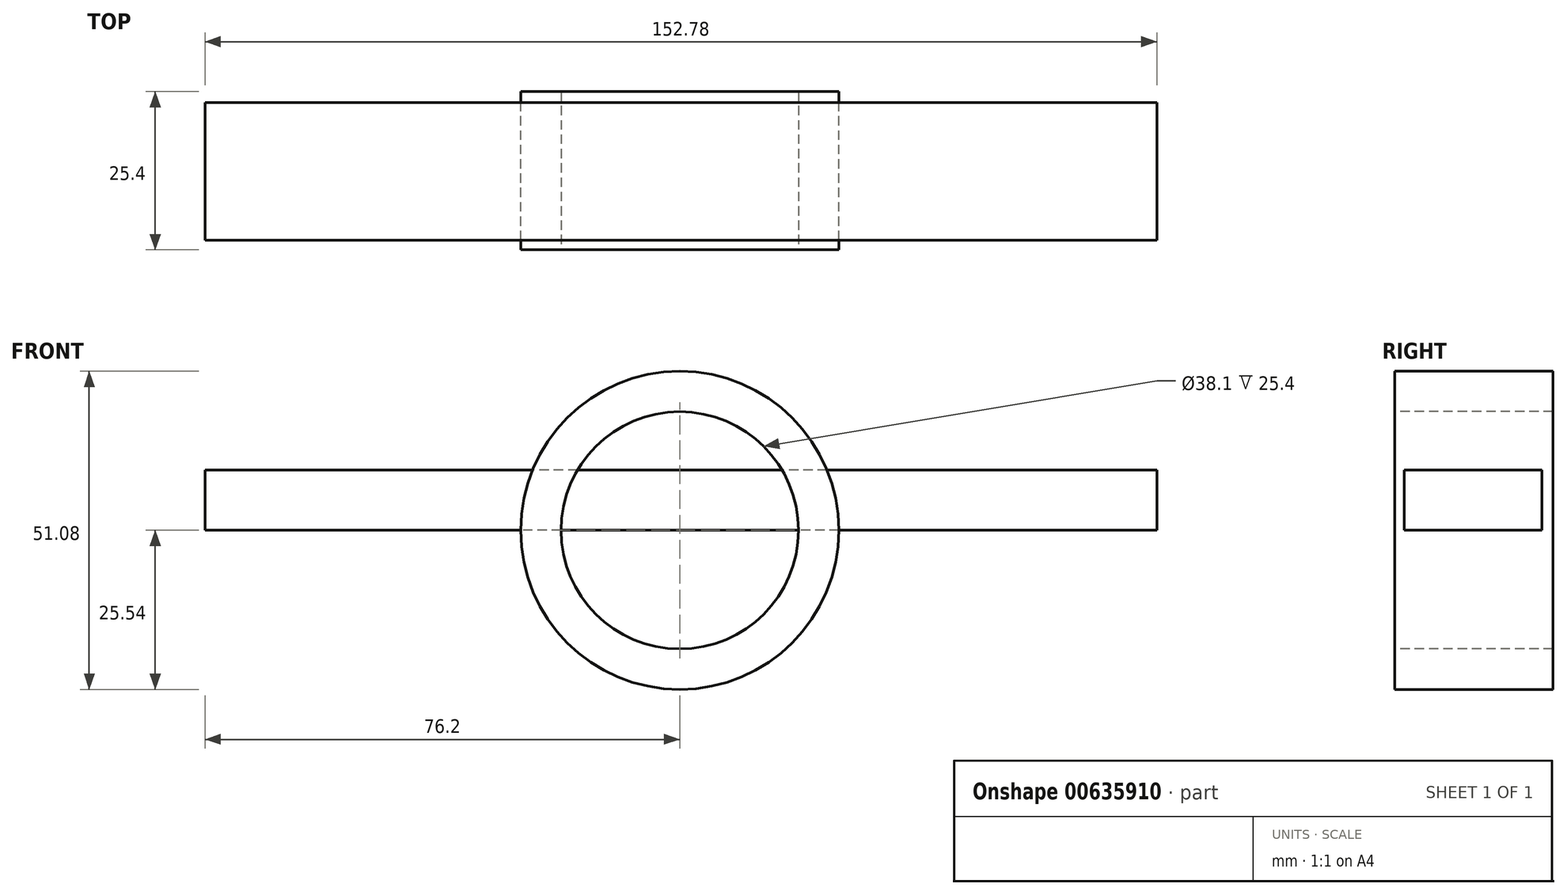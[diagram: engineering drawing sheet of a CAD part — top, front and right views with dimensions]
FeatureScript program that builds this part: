
annotation { "Feature Type Name" : "Feature", "Feature Type Description" : "" }
export const myFeature = defineFeature(function(context is Context, id is Id, definition is map)
    precondition{}
    {
        {
            var Q0;
            Q0=qCreatedBy(makeId("Front.planeOp"),FACE);
            var sketch = newSketch(context, id + "F0", { "sketchPlane" : qUnion([Q0])});
            skCircle(sketch, "E0", {"center": v(0, 0) * mm, "radius": 25.54 * mm});
            skSolve(sketch);
        }
        {
            var Q0;
            Q0=makeQuery(id+"F0.imprint","IMPRINT",FACE,{"disambiguationData":[TD([[makeQuery(id+"F0.imprint","IMPRINT",EDGE,{"derivedFrom":sQuery(id+"F0.wireOp",EDGE,"E0")}),1.0]])]});
            extrude(context, id + "F1", {"entities" : qUnion([Q0]), "depth" : 25.4 * mm, "offsetDistance" : 25.4 * mm});
        }
        {
            var Q0;
            Q0=makeQuery(id+"F1.opExtrude","CAP_FACE",FACE,{"disambiguationData":[OSD([sQuery(id+"F0.wireOp",EDGE,"E0")])],"isStart":false});
            var sketch = newSketch(context, id + "F2", { "sketchPlane" : qUnion([Q0])});
            skCircle(sketch, "E1", {"center": v(0, 0) * mm, "radius": 23.98 * mm});
            skSolve(sketch);
        }
        {
            var Q0;
            Q0=sQuery(id+"F2.wireOp",VERTEX,"E1.center");
            var Q1;
            Q1=makeQuery(id+"F1.opExtrude","SWEPT_BODY",BODY,{"disambiguationData":[OSD([sQuery(id+"F0.wireOp",EDGE,"E0")])]});
            hole(context, id + "F3", {"style" : HoleStyle.SIMPLE, "endStyle" : HoleEndStyle.THROUGH, "holeDiameter" : 38.1 * mm, "majorDiameter" : 6.35 * mm, "isTappedThrough" : true, "tappedDepth" : 12.7 * mm, "tapClearance" : 3, "locations" : qUnion([Q0]), "scope" : qUnion([Q1])});
        }
        {
            var Q0;
            Q0=qCreatedBy(makeId("Right.planeOp"),FACE);
            var sketch = newSketch(context, id + "F4", { "sketchPlane" : qUnion([Q0])});
            skLineSegment(sketch, "E2.bottom", {"start": v(-23.85, 9.65) * mm, "end": v(-1.8, 9.65) * mm});
            skLineSegment(sketch, "E2.top", {"start": v(-23.85, 0) * mm, "end": v(-1.8, 0) * mm});
            skLineSegment(sketch, "E2.left", {"start": v(-23.85, 9.65) * mm, "end": v(-23.85, 0) * mm});
            skLineSegment(sketch, "E2.right", {"start": v(-1.8, 9.65) * mm, "end": v(-1.8, 0) * mm});
            skSolve(sketch);
        }
        {
            var Q0;
            Q0=makeQuery(id+"F4.imprint","IMPRINT",FACE,{"disambiguationData":[TD([[makeQuery(id+"F4.imprint","IMPRINT",EDGE,{"derivedFrom":sQuery(id+"F4.wireOp",EDGE,"E2.bottom")}),-1.0]])]});
            extrude(context, id + "F5", {"entities" : qUnion([Q0]), "endBound" : BoundingType.THROUGH_ALL, "depth" : 25.4 * mm, "offsetDistance" : 25.4 * mm, "hasSecondDirection" : true, "secondDirectionOppositeDirection" : true, "secondDirectionDepth" : 76.2 * mm});
        }
    });
